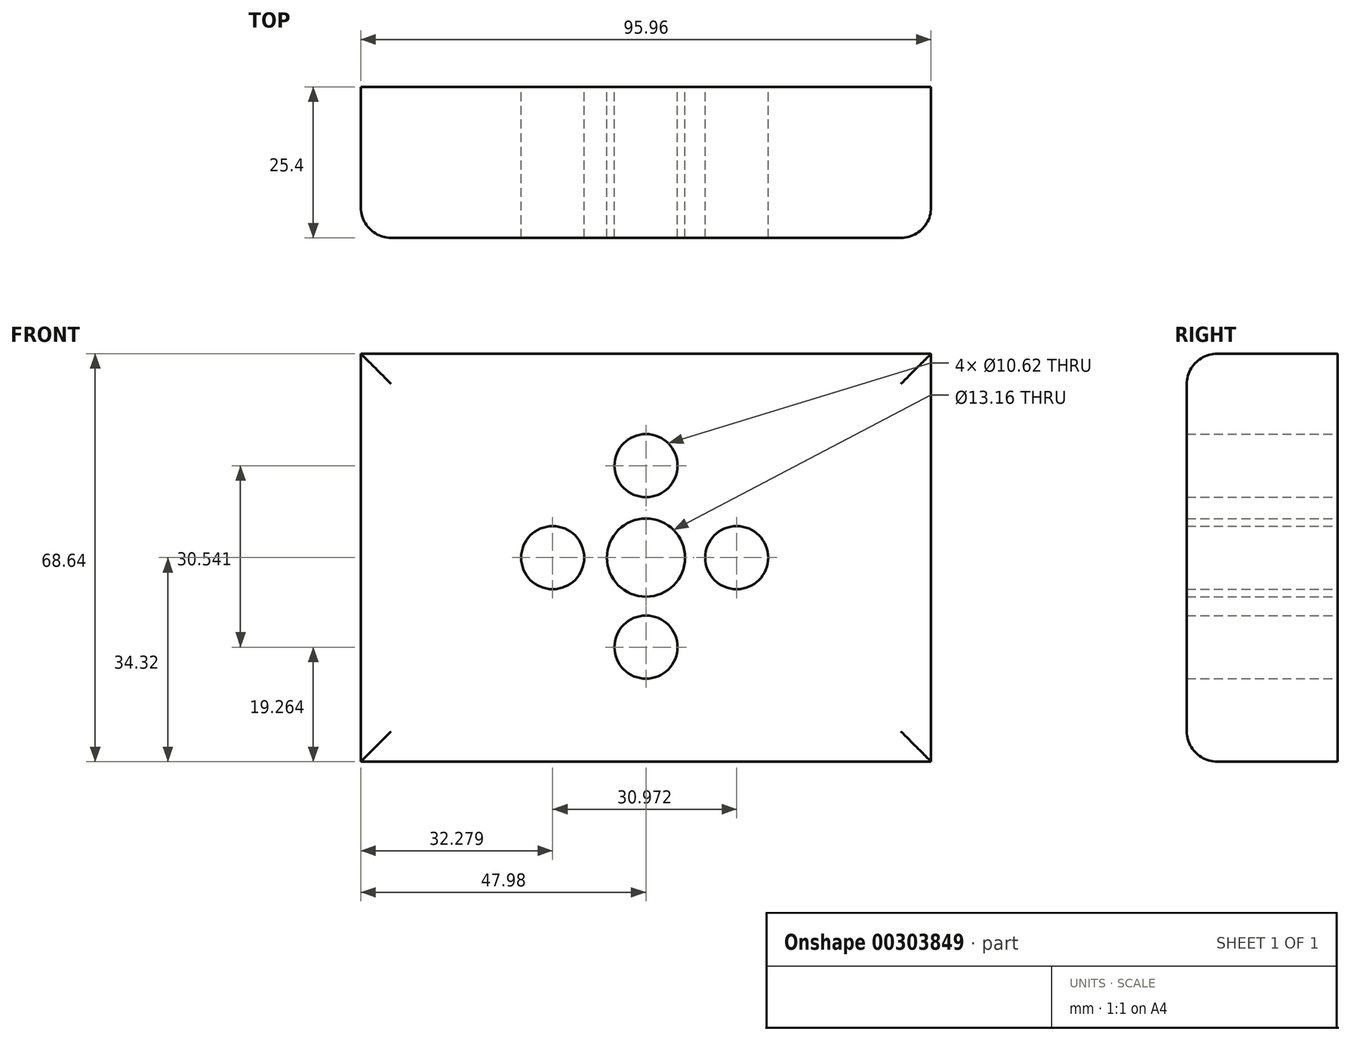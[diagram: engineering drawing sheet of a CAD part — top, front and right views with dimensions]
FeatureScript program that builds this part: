
annotation { "Feature Type Name" : "Feature", "Feature Type Description" : "" }
export const myFeature = defineFeature(function(context is Context, id is Id, definition is map)
    precondition{}
    {
        {
            var Q0;
            Q0=qCreatedBy(makeId("Front.planeOp"),FACE);
            var sketch = newSketch(context, id + "F0", { "sketchPlane" : qUnion([Q0])});
            skLineSegment(sketch, "E0.bottom", {"start": v(-47.98, 34.32) * mm, "end": v(47.98, 34.32) * mm});
            skLineSegment(sketch, "E0.top", {"start": v(-47.98, -34.32) * mm, "end": v(47.98, -34.32) * mm});
            skLineSegment(sketch, "E0.left", {"start": v(-47.98, 34.32) * mm, "end": v(-47.98, -34.32) * mm});
            skLineSegment(sketch, "E0.right", {"start": v(47.98, 34.32) * mm, "end": v(47.98, -34.32) * mm});
            skPoint(sketch, "E0.middle", {"position": v(0, 0) * mm});
            skCircle(sketch, "E1", {"center": v(0, 0) * mm, "radius": 6.58 * mm});
            skCircle(sketch, "E2", {"center": v(0, 15.49) * mm, "radius": 5.3 * mm});
            skCircle(sketch, "E3", {"center": v(15.27, 0) * mm, "radius": 5.3 * mm});
            skCircle(sketch, "E4", {"center": v(0, -15.06) * mm, "radius": 5.3 * mm});
            skCircle(sketch, "E5", {"center": v(-15.7, 0) * mm, "radius": 5.3 * mm});
            skPoint(sketch, "E6", {"position": v(-47.98, 34.32) * mm});
            skPoint(sketch, "E7", {"position": v(-47.98, -34.32) * mm});
            skPoint(sketch, "E8", {"position": v(47.98, -34.32) * mm});
            skPoint(sketch, "E9", {"position": v(47.98, 34.32) * mm});
            skSolve(sketch);
        }
        {
            var Q0;
            Q0=makeQuery(id+"F0.imprint","IMPRINT",FACE,{"disambiguationData":[TD([[makeQuery(id+"F0.imprint","IMPRINT",EDGE,{"derivedFrom":sQuery(id+"F0.wireOp",EDGE,"E0.bottom")}),-1.0]])]});
            extrude(context, id + "F1", {"entities" : qUnion([Q0]), "depth" : 25.4 * mm});
        }
        {
            var Q0;
            Q0=makeQuery(id+"F1.opExtrude","CAP_EDGE",EDGE,{"disambiguationData":[OSD([sQuery(id+"F0.wireOp",EDGE,"E0.bottom")])],"isStart":false});
            var Q1;
            Q1=makeQuery(id+"F1.opExtrude","CAP_EDGE",EDGE,{"disambiguationData":[OSD([sQuery(id+"F0.wireOp",EDGE,"E0.left")])],"isStart":false});
            var Q2;
            Q2=makeQuery(id+"F1.opExtrude","CAP_EDGE",EDGE,{"disambiguationData":[OSD([sQuery(id+"F0.wireOp",EDGE,"E0.top")])],"isStart":false});
            var Q3;
            Q3=makeQuery(id+"F1.opExtrude","CAP_EDGE",EDGE,{"disambiguationData":[OSD([sQuery(id+"F0.wireOp",EDGE,"E0.right")])],"isStart":false});
            fillet(context, id + "F2", {"entities" : qUnion([Q0, Q1, Q2, Q3]), "radius" : 5.08 * mm, "tangentPropagation" : true, "allowEdgeOverflow" : false});
        }
    });
